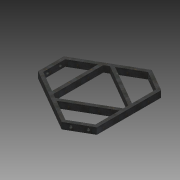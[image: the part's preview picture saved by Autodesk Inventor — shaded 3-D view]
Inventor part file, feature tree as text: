
AUTODESK INVENTOR PART (.ipt)
format: ipt  version: 2015 SP1 (Build 190203100, 203)  size: 153,600 bytes
history: native  units: in
note: dims shown in document units (in); Inventor stores cm internally (conversion verified against a paired STEP export)
features: extrude x4, sketch x4, projected_geometry x3
ambient origin geometry x8: Origin, YZ Plane, XZ Plane, XY Plane, X Axis, Y Axis, Z Axis, Center Point
bodies: Solid1 (feature_tree)
feature tree (11):
  extrude  "Extrusion1"  Depth=20.0in
  extrude  "Extrusion2"  Depth=15.5in
  extrude  "Extrusion3"  Depth=2.0in TaperAngle=0.0deg
  extrude  "Extrusion4"  Depth=2.0in
  sketch  "Sketch1"  dims[d0=8.0in d6=20.0in]
  sketch  "Sketch2"  dims[d14=15.5in d16=15.5in]
  projected_geometry  "Projected Loop1"
  sketch  "Sketch3"  dims[d17=15.5in d21=2.0in d22=0.0in]
  projected_geometry  "Projected Loop2"
  sketch  "Sketch4"  dims[d23=2.0in d24=2.0in d25=0.875in d26=0.875in d27=1.0in d28=0.0in d29=2.0in d30=2.0in d31=0.875in d32=0.875in d33=1.0in d34=0.0in d35=2.0in d36=2.0in d37=0.875in d38=0.875in d39=1.0in d40=0.0in]
  projected_geometry  "Projected Loop3"
